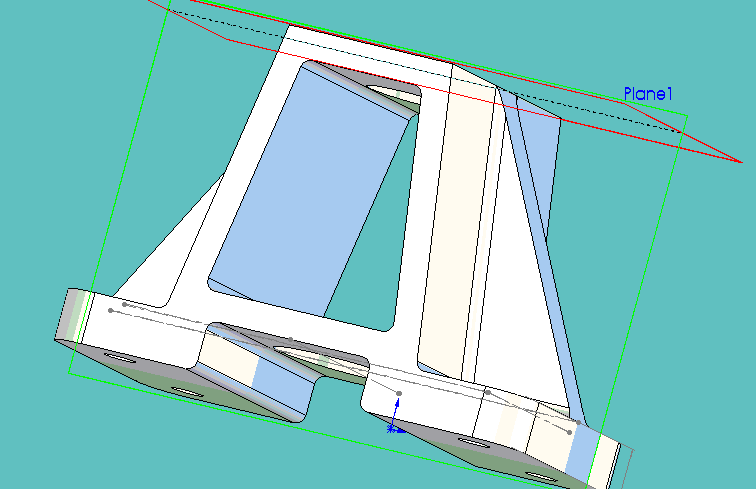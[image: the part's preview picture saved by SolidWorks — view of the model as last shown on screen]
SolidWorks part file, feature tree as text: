
SOLIDWORKS PART (.sldprt)
format: sldprt  version: not decoded by parser v0  size: 470,528 bytes
history: native  units: mm
features: sketch x15, cut_extrude x8, plane x5, fillet x5, extrude x3, material x1, shell x1, pattern_linear x1 + 1 further entry (+9 scaffold rows collapsed)
feature tree (49):
  "Annotations"  RD1=11.938mm
  scaffold x9  (default folders/planes/origin — collapsed)
  material  "Material <not specified>"
  plane  "Frontal"
  plane  "Horizontal"
  plane  "Profile"
  sketch  "Sketch1"  dims[D1=72.644mm D2=116.586mm]
  extrude  "Extrude1"  Depth=11.938mm
  sketch  "Sketch2"  dims[D1=13.716mm D2=14.224mm]
  cut_extrude  "Cut-Extrude1"  [1 undecoded]
  sketch  "Sketch4"  dims[D1=~14.159943mm]
  plane  "Plane1"  Offset=81.026mm
  sketch  "Sketch5"  dims[D1=40.64mm]
  extrude  "Extrude3"  Depth=69.088mm
  sketch  "Sketch6"  dims[D1=40.64mm]
  cut_extrude  "Cut-Extrude3"  Depth=11.938mm
  sketch  "Sketch7"
  cut_extrude  "Cut-Extrude4"  [1 undecoded]
  sketch  "Sketch8"
  cut_extrude  "Cut-Extrude5"  [1 undecoded]
  shell  "Shell1"  Thickness=6.604mm
  sketch  "Sketch9"  dims[D1=~12.613299mm]
  cut_extrude  "Cut-Extrude6"  [1 undecoded]
  sketch  "Sketch10"  dims[D1=~8.549328mm]
  cut_extrude  "Cut-Extrude7"  [1 undecoded]
  sketch  "Sketch14"
  extrude  "Extrude5"  Depth=11.938mm
  sketch  "Sketch15"  dims[D3=~6.447274mm D1=13.716mm D2=14.224mm]
  cut_extrude  "Cut-Extrude10"  [1 undecoded]
  sketch  "Sketch16"  dims[D1=~7.960733mm]
  cut_extrude  "Cut-Extrude11"  Depth=4.826mm
  sketch  "Sketch17"
  pattern_linear  "LPattern2"  Count1=2 Count2=2 Spacing1=45.212mm Spacing2=88.138mm
  fillet  "Fillet1"  Radius=9.652mm
  fillet  "Fillet2"  Radius=2.286mm
  fillet  "Fillet3"  Radius=2.286mm
  plane  "Plane2"  Offset=7.3152mm
  sketch  "Sketch21"  dims[D1=9.652mm]
  sketch  "Sketch22"  dims[D1=9.652mm]
  fillet  "Fillet4"  Radius=2.286mm
  fillet  "Fillet5"  Radius=2.286mm
decode coverage: 23 of 33 modeling features carry decoded parameters; 1 rows unclassified (native names shown)
note: ~ marks probable driven/reference dimensions
note: 6 parameter values undecoded
summary: no parameter record found for 6 features
note: suppression state not decoded; provenance and decode notes live in map.json
